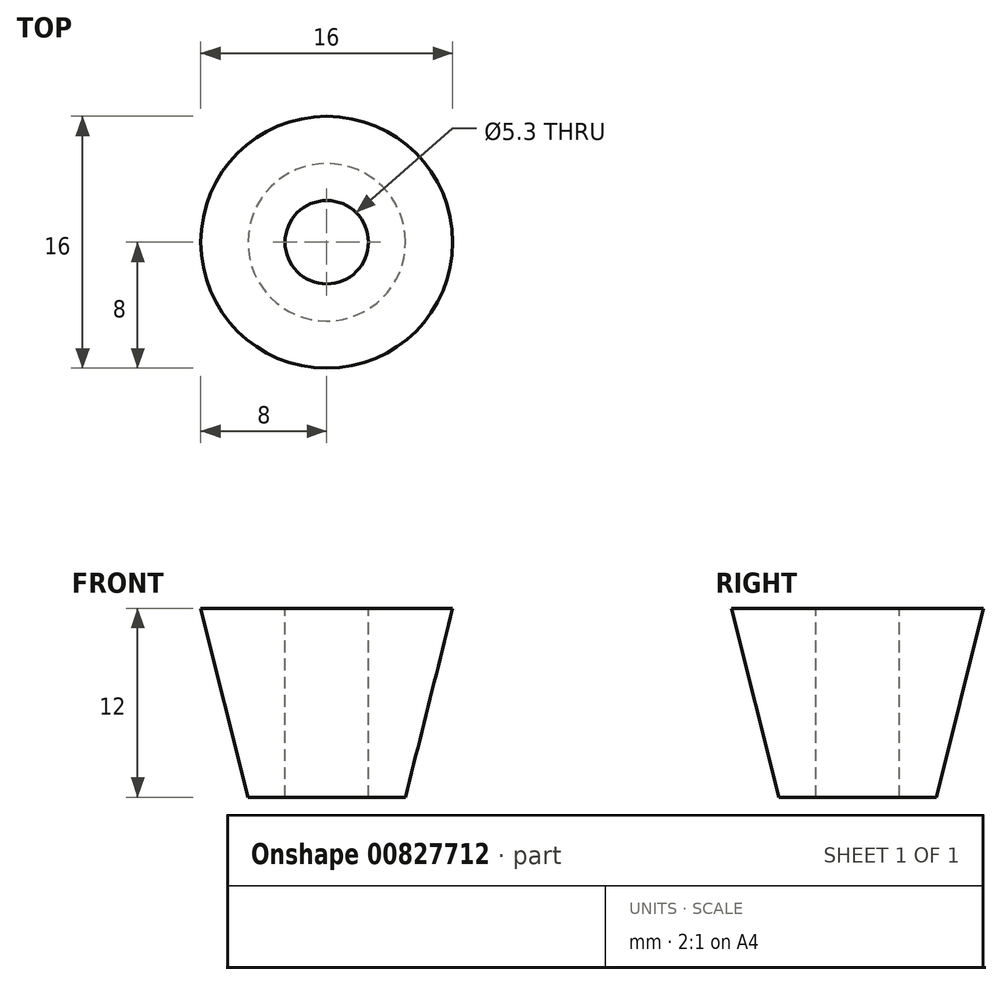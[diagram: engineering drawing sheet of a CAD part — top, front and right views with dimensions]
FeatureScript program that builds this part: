
annotation { "Feature Type Name" : "Feature", "Feature Type Description" : "" }
export const myFeature = defineFeature(function(context is Context, id is Id, definition is map)
    precondition{}
    {
        {
            var Q0;
            Q0=qCreatedBy(makeId("Top.planeOp"),FACE);
            var sketch = newSketch(context, id + "F0", { "sketchPlane" : qUnion([Q0])});
            skCircle(sketch, "E0", {"center": v(0, 0) * mm, "radius": 5 * mm});
            skSolve(sketch);
        }
        {
            var Q0;
            Q0=qCreatedBy(makeId("Top.planeOp"),FACE);
            cPlane(context, id + "F1", {"entities" : qUnion([Q0]), "cplaneType" : CPlaneType.OFFSET, "offset" : 12 * mm, "width" : 150 * mm, "height" : 150 * mm});
        }
        {
            var Q0;
            Q0=qCreatedBy(id+"F1.planeOp",FACE);
            var sketch = newSketch(context, id + "F2", { "sketchPlane" : qUnion([Q0])});
            skPoint(sketch, "E1.0", {"position": v(0, 0) * mm});
            skCircle(sketch, "E2", {"center": v(0, 0) * mm, "radius": 8 * mm});
            skSolve(sketch);
        }
        {
            var Q0;
            Q0=makeQuery(id+"F0.imprint","IMPRINT",FACE,{"disambiguationData":[TD([[makeQuery(id+"F0.imprint","IMPRINT",EDGE,{"derivedFrom":sQuery(id+"F0.wireOp",EDGE,"E0")}),1.0]])]});
            var Q1;
            Q1=makeQuery(id+"F2.imprint","IMPRINT",FACE,{"disambiguationData":[TD([[makeQuery(id+"F2.imprint","IMPRINT",EDGE,{"derivedFrom":sQuery(id+"F2.wireOp",EDGE,"E2")}),1.0]])]});
            loft(context, id + "F3", {"sheetProfilesArray" : [{ "sheetProfileEntities" : qUnion([Q0]) }, { "sheetProfileEntities" : qUnion([Q1]) }]});
        }
        {
            var Q0;
            Q0=sQuery(id+"F0.wireOp",VERTEX,"E0.center");
            var Q1;
            Q1=makeQuery(id+"F3.opLoft","SWEPT_BODY",BODY,{"disambiguationData":[OSD([makeQuery(id+"F0.imprint","IMPRINT",FACE,{"disambiguationData":[TD([[makeQuery(id+"F0.imprint","IMPRINT",EDGE,{"derivedFrom":sQuery(id+"F0.wireOp",EDGE,"E0")}),1.0]])]}),makeQuery(id+"F2.imprint","IMPRINT",FACE,{"disambiguationData":[TD([[makeQuery(id+"F2.imprint","IMPRINT",EDGE,{"derivedFrom":sQuery(id+"F2.wireOp",EDGE,"E2")}),1.0]])]})])]});
            hole(context, id + "F4", {"style" : HoleStyle.SIMPLE, "endStyle" : HoleEndStyle.BLIND, "oppositeDirection" : true, "holeDiameter" : 5.3 * mm, "majorDiameter" : 5 * mm, "holeDepth" : 90 * mm, "isTappedThrough" : true, "tappedDepth" : 12 * mm, "tapClearance" : 3, "locations" : qUnion([Q0]), "scope" : qUnion([Q1]), "startStyle" : HoleStartStyle.PART});
        }
    });
